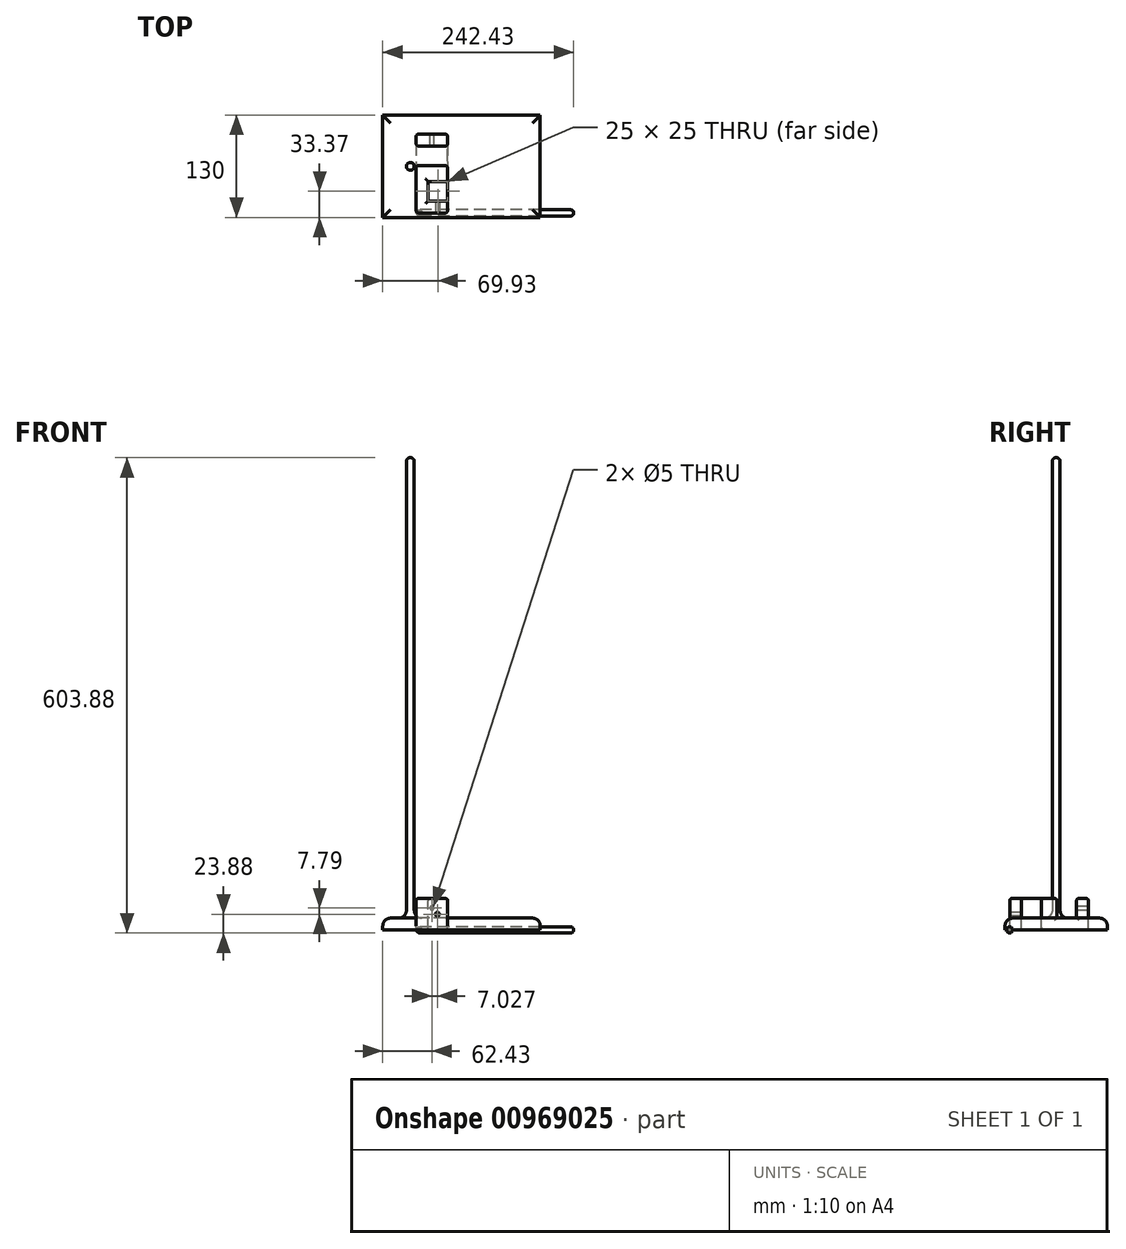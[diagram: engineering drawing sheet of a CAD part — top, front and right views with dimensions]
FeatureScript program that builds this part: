
annotation { "Feature Type Name" : "Feature", "Feature Type Description" : "" }
export const myFeature = defineFeature(function(context is Context, id is Id, definition is map)
    precondition{}
    {
        {
            var Q0;
            Q0=qCreatedBy(makeId("Top.planeOp"),FACE);
            var sketch = newSketch(context, id + "F0", { "sketchPlane" : qUnion([Q0])});
            skLineSegment(sketch, "E0.bottom", {"start": v(157.57, -5.87) * mm, "end": v(-42.43, -5.87) * mm});
            skLineSegment(sketch, "E0.top", {"start": v(157.57, 124.13) * mm, "end": v(-42.43, 124.13) * mm});
            skLineSegment(sketch, "E0.left", {"start": v(157.57, -5.87) * mm, "end": v(157.57, 124.13) * mm});
            skLineSegment(sketch, "E0.right", {"start": v(-42.43, -5.87) * mm, "end": v(-42.43, 124.13) * mm});
            skCircle(sketch, "E1", {"center": v(-7.43, 59.13) * mm, "radius": 5 * mm});
            skSolve(sketch);
        }
        {
            var Q0;
            Q0 = qSketchRegion(id + "F0", true);
            extrude(context, id + "F1", {"entities" : qUnion([Q0]), "depth" : 15 * mm, "offsetDistance" : 25.4 * mm});
        }
        {
            var Q0;
            Q0=makeQuery(id+"F0.imprint","IMPRINT",FACE,{"disambiguationData":[TD([[makeQuery(id+"F0.imprint","IMPRINT",EDGE,{"derivedFrom":sQuery(id+"F0.wireOp",EDGE,"E1")}),1.0]])]});
            extrude(context, id + "F2", {"entities" : qUnion([Q0]), "operationType" : NewBodyOperationType.ADD, "depth" : 600 * mm, "offsetDistance" : 25.4 * mm});
        }
        {
            var Q0;
            Q0=makeQuery(id+"F1.opExtrude","CAP_FACE",FACE,{"disambiguationData":[OSD([sQuery(id+"F0.wireOp",EDGE,"E0.bottom"),sQuery(id+"F0.wireOp",EDGE,"E0.top"),sQuery(id+"F0.wireOp",EDGE,"E0.left"),sQuery(id+"F0.wireOp",EDGE,"E0.right"),sQuery(id+"F0.wireOp",EDGE,"E1")])],"isStart":false});
            fillet(context, id + "F3", {"entities" : qUnion([Q0]), "radius" : 10 * mm, "tangentPropagation" : true, "allowEdgeOverflow" : false});
        }
        {
            var Q0;
            Q0=makeQuery(id+"F2.opExtrude","CAP_FACE",FACE,{"disambiguationData":[OSD([sQuery(id+"F0.wireOp",EDGE,"E1")])],"isStart":false});
            fillet(context, id + "F4", {"entities" : qUnion([Q0]), "radius" : 4.9 * mm, "allowEdgeOverflow" : false});
        }
        {
            var Q0;
            Q0=qCreatedBy(makeId("Right.planeOp"),FACE);
            var sketch = newSketch(context, id + "F5", { "sketchPlane" : qUnion([Q0])});
            skLineSegment(sketch, "E2.bottom", {"start": v(0, 0) * mm, "end": v(100, 0) * mm});
            skLineSegment(sketch, "E2.top", {"start": v(0, 40) * mm, "end": v(100, 40) * mm});
            skLineSegment(sketch, "E2.left", {"start": v(0, 0) * mm, "end": v(0, 40) * mm});
            skLineSegment(sketch, "E2.right", {"start": v(100, 0) * mm, "end": v(100, 40) * mm});
            skLineSegment(sketch, "E3", {"start": v(85, 40) * mm, "end": v(85, 15) * mm});
            skLineSegment(sketch, "E4", {"start": v(85, 15) * mm, "end": v(60, 15) * mm});
            skLineSegment(sketch, "E5", {"start": v(60, 15) * mm, "end": v(60, 40) * mm});
            skSolve(sketch);
        }
        {
            var Q0;
            Q0=makeQuery(id+"F5.imprint","IMPRINT",FACE,{"disambiguationData":[TD([[makeQuery(id+"F5.imprint","IMPRINT",EDGE,{"derivedFrom":sQuery(id+"F5.wireOp",EDGE,"E2.bottom")}),1.0]])]});
            extrude(context, id + "F6", {"entities" : qUnion([Q0]), "depth" : 40 * mm, "offsetDistance" : 25 * mm});
        }
        {
            var Q0;
            Q0=makeQuery(id+"F6.opExtrude","SWEPT_FACE",FACE,{"disambiguationData":[OSD([sQuery(id+"F5.wireOp",EDGE,"E2.top")])]});
            var sketch = newSketch(context, id + "F7", { "sketchPlane" : qUnion([Q0])});
            skLineSegment(sketch, "E6", {"start": v(40, 15) * mm, "end": v(15, 15) * mm});
            skLineSegment(sketch, "E7", {"start": v(15, 15) * mm, "end": v(15, 40) * mm});
            skLineSegment(sketch, "E8", {"start": v(15, 40) * mm, "end": v(40, 40) * mm});
            skLineSegment(sketch, "E9", {"start": v(40, 40) * mm, "end": v(40, 15) * mm});
            skSolve(sketch);
        }
        {
            var Q0;
            Q0=makeQuery(id+"F7.imprint","IMPRINT",FACE,{"disambiguationData":[TD([[makeQuery(id+"F7.imprint","IMPRINT",EDGE,{"derivedFrom":sQuery(id+"F7.wireOp",EDGE,"E6")}),-1.0]])]});
            extrude(context, id + "F8", {"entities" : qUnion([Q0]), "operationType" : NewBodyOperationType.REMOVE, "oppositeDirection" : true, "depth" : 40 * mm, "offsetDistance" : 25 * mm});
        }
        {
            var Q0;
            Q0=makeQuery(id+"F6.opExtrude","SWEPT_FACE",FACE,{"disambiguationData":[OSD([sQuery(id+"F5.wireOp",EDGE,"E2.left")])]});
            var sketch = newSketch(context, id + "F9", { "sketchPlane" : qUnion([Q0])});
            skLineSegment(sketch, "E10", {"start": v(0, 20) * mm, "end": v(40, 20) * mm, "construction": true});
            skPoint(sketch, "E11", {"position": v(27.03, 20) * mm});
            skSolve(sketch);
        }
        {
            var Q0;
            Q0=sQuery(id+"F9.wireOp",VERTEX,"E11");
            var Q1;
            Q1=makeQuery(id+"F6.opExtrude","SWEPT_BODY",BODY,{"disambiguationData":[OSD([sQuery(id+"F5.wireOp",EDGE,"E2.bottom"),sQuery(id+"F5.wireOp",EDGE,"E2.top"),sQuery(id+"F5.wireOp",EDGE,"E2.left"),sQuery(id+"F5.wireOp",EDGE,"E2.right")])]});
            hole(context, id + "F10", {"style" : HoleStyle.SIMPLE, "endStyle" : HoleEndStyle.BLIND, "standardTappedOrClearance" : lookupTablePath({ "standard" : "ISO", "engagement" : "75%", "pitch" : "1 mm", "size" : "M6", "type" : "Tapped" }), "standardBlindInLast" : lookupTablePath({ "standard" : "ISO", "fit" : "Normal", "engagement" : "75%", "pitch" : "1 mm", "size" : "M6", "type" : "Clearance & tapped" }), "holeDiameter" : 5 * mm, "majorDiameter" : 6 * mm, "showTappedDepth" : true, "holeDepth" : 15 * mm, "isTappedThrough" : true, "tappedDepth" : 12 * mm, "tapClearance" : 3, "locations" : qUnion([Q0]), "scope" : qUnion([Q1])});
        }
        {
            var Q0;
            Q0=makeQuery(id+"F6.opExtrude","SWEPT_FACE",FACE,{"disambiguationData":[OSD([sQuery(id+"F5.wireOp",EDGE,"E2.right")])]});
            var sketch = newSketch(context, id + "F11", { "sketchPlane" : qUnion([Q0])});
            skLineSegment(sketch, "E12", {"start": v(-20, 0) * mm, "end": v(-20, 40) * mm, "construction": true});
            skPoint(sketch, "E13", {"position": v(-20, 27.79) * mm});
            skSolve(sketch);
        }
        {
            var Q0;
            Q0=sQuery(id+"F11.wireOp",VERTEX,"E13");
            var Q1;
            Q1=makeQuery(id+"F6.opExtrude","SWEPT_BODY",BODY,{"disambiguationData":[OSD([sQuery(id+"F5.wireOp",EDGE,"E2.bottom"),sQuery(id+"F5.wireOp",EDGE,"E2.top"),sQuery(id+"F5.wireOp",EDGE,"E2.left"),sQuery(id+"F5.wireOp",EDGE,"E2.right"),sQuery(id+"F5.wireOp",EDGE,"E3"),sQuery(id+"F5.wireOp",EDGE,"E4"),sQuery(id+"F5.wireOp",EDGE,"E5")])]});
            hole(context, id + "F12", {"style" : HoleStyle.SIMPLE, "endStyle" : HoleEndStyle.BLIND, "standardTappedOrClearance" : lookupTablePath({ "standard" : "ISO", "engagement" : "75%", "pitch" : "1 mm", "size" : "M6", "type" : "Tapped" }), "standardBlindInLast" : lookupTablePath({ "standard" : "ISO", "fit" : "Normal", "engagement" : "75%", "pitch" : "1 mm", "size" : "M6", "type" : "Clearance & tapped" }), "holeDiameter" : 5 * mm, "majorDiameter" : 6 * mm, "showTappedDepth" : true, "holeDepth" : 15 * mm, "isTappedThrough" : true, "tappedDepth" : 12 * mm, "tapClearance" : 3, "locations" : qUnion([Q0]), "scope" : qUnion([Q1])});
        }
        {
            var Q0;
            {var subQ0=sQuery(id+"F5.wireOp",EDGE,"E2.top");Q0=makeQuery(id+"F6.opExtrude","SWEPT_FACE",FACE,{"disambiguationData":[OSD([subQ0]),TDD([makeQuery(id+"F5.imprint","IMPRINT",EDGE,{"disambiguationData":[TD([[makeQuery(id+"F5.imprint","INTERSECT",VERTEX,{"derivedFrom":[subQ0,sQuery(id+"F5.wireOp",EDGE,"E2.left")]}),-1.0]])],"derivedFrom":subQ0})])]});}
            var Q1;
            {var subQ0=sQuery(id+"F5.wireOp",EDGE,"E2.top");Q1=makeQuery(id+"F6.opExtrude","SWEPT_FACE",FACE,{"disambiguationData":[OSD([subQ0]),TDD([makeQuery(id+"F5.imprint","IMPRINT",EDGE,{"disambiguationData":[TD([[makeQuery(id+"F5.imprint","INTERSECT",VERTEX,{"derivedFrom":[subQ0,sQuery(id+"F5.wireOp",EDGE,"E2.right")]}),1.0]])],"derivedFrom":subQ0})])]});}
            var Q2;
            Q2=makeQuery(id+"F6.opExtrude","CAP_FACE",FACE,{"disambiguationData":[OSD([sQuery(id+"F5.wireOp",EDGE,"E2.bottom"),sQuery(id+"F5.wireOp",EDGE,"E2.top"),sQuery(id+"F5.wireOp",EDGE,"E2.left"),sQuery(id+"F5.wireOp",EDGE,"E2.right"),sQuery(id+"F5.wireOp",EDGE,"E3"),sQuery(id+"F5.wireOp",EDGE,"E4"),sQuery(id+"F5.wireOp",EDGE,"E5")])],"isStart":true});
            var Q3;
            Q3=makeQuery(id+"F6.opExtrude","SWEPT_FACE",FACE,{"disambiguationData":[OSD([sQuery(id+"F5.wireOp",EDGE,"E2.bottom")])]});
            var Q4;
            {var subQ0=sQuery(id+"F5.wireOp",EDGE,"E2.bottom");var subQ1=sQuery(id+"F5.wireOp",EDGE,"E2.left");var subQ2=sQuery(id+"F5.wireOp",EDGE,"E2.top");var subQ3=sQuery(id+"F5.wireOp",EDGE,"E5");Q4=makeQuery(id+"F8.boolean.opBoolean","SPLIT",FACE,{"disambiguationData":[TD([makeQuery(id+"F6.opExtrude","SWEPT_FACE",FACE,{"disambiguationData":[OSD([subQ1])]})])],"derivedFrom":makeQuery(id+"F6.opExtrude","CAP_FACE",FACE,{"disambiguationData":[OSD([subQ0,subQ2,subQ1,sQuery(id+"F5.wireOp",EDGE,"E2.right"),sQuery(id+"F5.wireOp",EDGE,"E3"),sQuery(id+"F5.wireOp",EDGE,"E4"),subQ3])],"isStart":false})});}
            var Q5;
            {var subQ0=sQuery(id+"F5.wireOp",EDGE,"E2.right");var subQ1=sQuery(id+"F5.wireOp",EDGE,"E2.top");var subQ2=sQuery(id+"F5.wireOp",EDGE,"E3");var subQ3=sQuery(id+"F5.wireOp",EDGE,"E2.left");var subQ4=sQuery(id+"F5.wireOp",EDGE,"E5");var subQ5=sQuery(id+"F5.wireOp",EDGE,"E2.bottom");var subQ6=sQuery(id+"F5.wireOp",EDGE,"E4");Q5=makeQuery(id+"F8.boolean.opBoolean","SPLIT",FACE,{"disambiguationData":[TD([makeQuery(id+"F6.opExtrude","SWEPT_FACE",FACE,{"disambiguationData":[OSD([subQ0])]})])],"derivedFrom":makeQuery(id+"F6.opExtrude","CAP_FACE",FACE,{"disambiguationData":[OSD([subQ5,subQ1,subQ3,subQ0,subQ2,subQ6,subQ4])],"isStart":false})});}
            fillet(context, id + "F13", {"entities" : qUnion([Q0, Q1, Q2, Q3, Q4, Q5]), "radius" : 3 * mm, "tangentPropagation" : true, "allowEdgeOverflow" : false});
        }
        {
            var Q0;
            Q0=qCreatedBy(makeId("Right.planeOp"),FACE);
            var sketch = newSketch(context, id + "F14", { "sketchPlane" : qUnion([Q0])});
            skCircle(sketch, "E14", {"center": v(0, 0) * mm, "radius": 3.88 * mm});
            skSolve(sketch);
        }
        {
            var Q0;
            Q0=makeQuery(id+"F14.imprint","IMPRINT",FACE,{"disambiguationData":[TD([[makeQuery(id+"F14.imprint","IMPRINT",EDGE,{"derivedFrom":sQuery(id+"F14.wireOp",EDGE,"E14")}),1.0]])]});
            extrude(context, id + "F15", {"entities" : qUnion([Q0]), "depth" : 200 * mm, "offsetDistance" : 25 * mm});
        }
        {
            var Q0;
            Q0=makeQuery(id+"F15.opExtrude","CAP_FACE",FACE,{"disambiguationData":[OSD([sQuery(id+"F14.wireOp",EDGE,"E14")])],"isStart":true});
            var Q1;
            Q1=makeQuery(id+"F15.opExtrude","CAP_FACE",FACE,{"disambiguationData":[OSD([sQuery(id+"F14.wireOp",EDGE,"E14")])],"isStart":false});
            fillet(context, id + "F16", {"entities" : qUnion([Q0, Q1]), "radius" : 3.5 * mm, "tangentPropagation" : true, "allowEdgeOverflow" : false});
        }
    });
